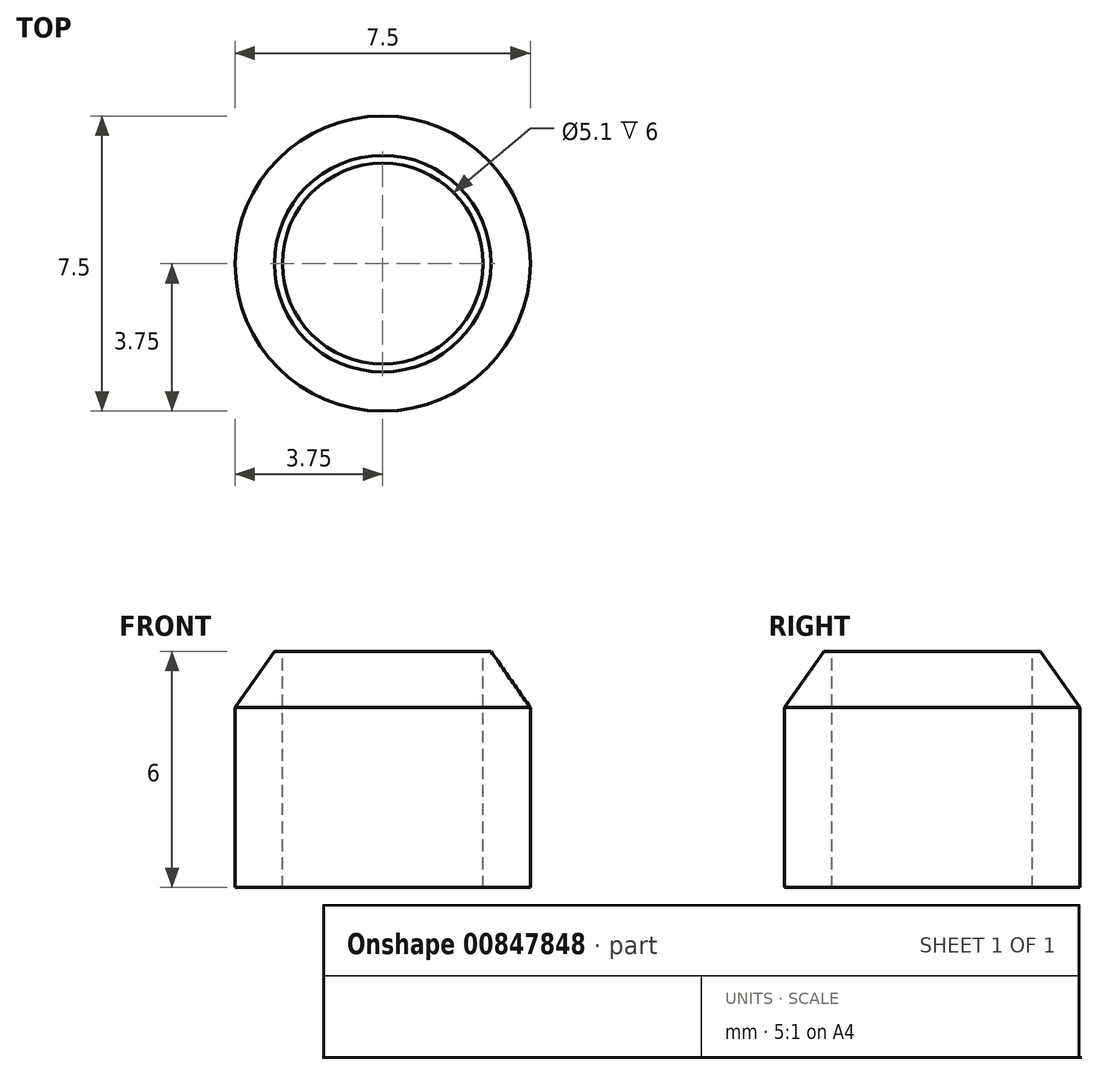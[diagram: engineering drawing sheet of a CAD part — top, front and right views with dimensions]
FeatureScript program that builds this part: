
annotation { "Feature Type Name" : "Feature", "Feature Type Description" : "" }
export const myFeature = defineFeature(function(context is Context, id is Id, definition is map)
    precondition{}
    {
        {
            var Q0;
            Q0=qCreatedBy(makeId("Top.planeOp"),FACE);
            var sketch = newSketch(context, id + "F0", { "sketchPlane" : qUnion([Q0])});
            skCircle(sketch, "E0", {"center": v(0, 0) * mm, "radius": 3.75 * mm});
            skSolve(sketch);
        }
        {
            var Q0;
            Q0=makeQuery(id+"F0.imprint","IMPRINT",FACE,{"disambiguationData":[TD([[makeQuery(id+"F0.imprint","IMPRINT",EDGE,{"derivedFrom":sQuery(id+"F0.wireOp",EDGE,"E0")}),1.0]])]});
            extrude(context, id + "F1", {"entities" : qUnion([Q0]), "depth" : 6 * mm, "offsetDistance" : 25 * mm});
        }
        {
            var Q0;
            Q0=makeQuery(id+"F1.opExtrude","CAP_FACE",FACE,{"disambiguationData":[OSD([sQuery(id+"F0.wireOp",EDGE,"E0")])],"isStart":false});
            var sketch = newSketch(context, id + "F2", { "sketchPlane" : qUnion([Q0])});
            skCircle(sketch, "E1", {"center": v(0, 0) * mm, "radius": 2.55 * mm});
            skSolve(sketch);
        }
        {
            var Q0;
            Q0=makeQuery(id+"F2.imprint","IMPRINT",FACE,{"disambiguationData":[TD([[makeQuery(id+"F2.imprint","IMPRINT",EDGE,{"derivedFrom":sQuery(id+"F2.wireOp",EDGE,"E1")}),1.0]])]});
            extrude(context, id + "F3", {"entities" : qUnion([Q0]), "operationType" : NewBodyOperationType.REMOVE, "endBound" : BoundingType.UP_TO_NEXT, "oppositeDirection" : true, "depth" : 25 * mm, "offsetDistance" : 25 * mm});
        }
        {
            var Q0;
            Q0=makeQuery(id+"F1.opExtrude","CAP_EDGE",EDGE,{"disambiguationData":[OSD([sQuery(id+"F0.wireOp",EDGE,"E0")])],"isStart":false});
            chamfer(context, id + "F4", {"entities" : qUnion([Q0]), "chamferType" : ChamferType.OFFSET_ANGLE, "width" : (1) * mm, "oppositeDirection" : false, "angle" : 55 * degree, "tangentPropagation" : true});
        }
    });
